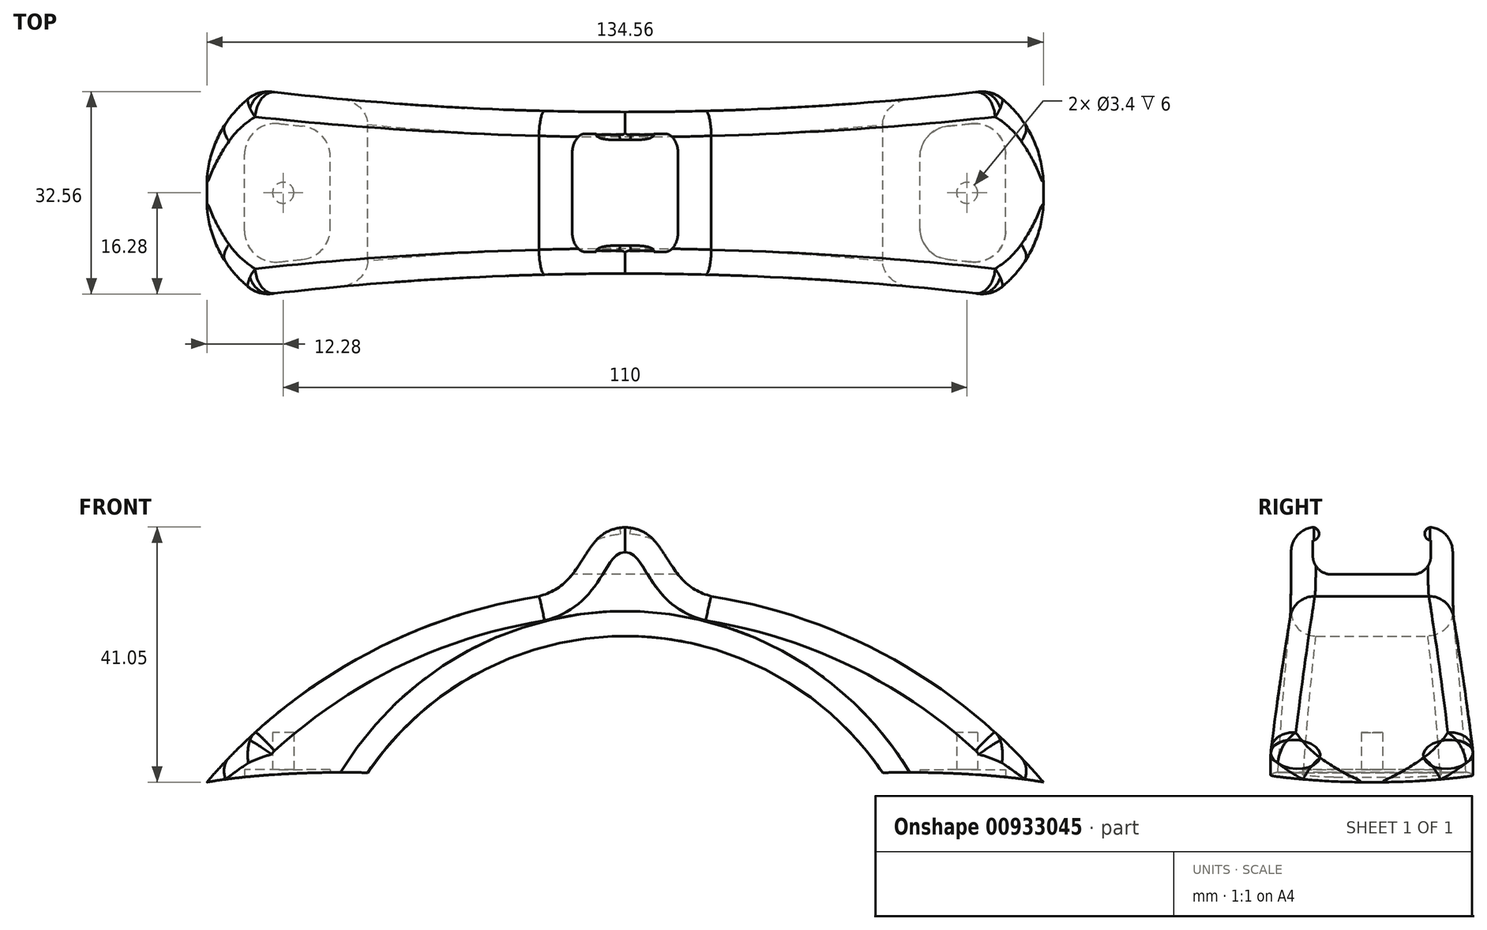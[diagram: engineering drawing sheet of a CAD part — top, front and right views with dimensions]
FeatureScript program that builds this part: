
annotation { "Feature Type Name" : "Feature", "Feature Type Description" : "" }
export const myFeature = defineFeature(function(context is Context, id is Id, definition is map)
    precondition{}
    {
        {
            var Q0;
            Q0=qCreatedBy(makeId("Front.planeOp"),FACE);
            var sketch = newSketch(context, id + "F0", { "sketchPlane" : qUnion([Q0])});
            skCircle(sketch, "E0", {"center": v(0, -26.5) * mm, "radius": 50 * mm});
            skCircle(sketch, "E1", {"center": v(0, -57.5) * mm, "radius": 88.5 * mm});
            skSolve(sketch);
        }
        {
            var Q0;
            Q0 = qSketchRegion(id + "F0", true);
            var Q1;
            Q1 = qSketchRegion(id + "F2", true);
            extrude(context, id + "F1", {"entities" : qUnion([Q0, Q1]), "flatOperationType" : FlatOperationType.REMOVE, "endBound" : BoundingType.SYMMETRIC, "depth" : 35 * mm, "offsetDistance" : 25 * mm, "domain" : OperationDomain.MODEL});
        }
        {
            var Q0;
            Q0=qCreatedBy(makeId("Top.planeOp"),FACE);
            var sketch = newSketch(context, id + "F2", { "sketchPlane" : qUnion([Q0])});
            skLineSegment(sketch, "E2.bottom", {"start": v(69.4, -44.81) * mm, "end": v(-70.4, -44.81) * mm});
            skLineSegment(sketch, "E2.top", {"start": v(69.4, 50.02) * mm, "end": v(-70.4, 50.02) * mm});
            skLineSegment(sketch, "E2.left", {"start": v(69.4, -44.81) * mm, "end": v(69.4, 50.02) * mm});
            skLineSegment(sketch, "E2.right", {"start": v(-70.4, -44.81) * mm, "end": v(-70.4, 50.02) * mm});
            skSolve(sketch);
        }
        {
            var Q0;
            Q0 = qSketchRegion(id + "F2", true);
            extrude(context, id + "F3", {"entities" : qUnion([Q0]), "operationType" : NewBodyOperationType.INTERSECT, "depth" : 50 * mm, "offsetDistance" : 25 * mm});
        }
        {
            var Q0;
            Q0=qCreatedBy(makeId("Top.planeOp"),FACE);
            var sketch = newSketch(context, id + "F4", { "sketchPlane" : qUnion([Q0])});
            skArc(sketch, "E3", {"start": v(-67.28, 0) * mm, "mid": v(-64.75, -10.32) * mm, "end": v(-56.92, -17.5) * mm});
            skLineSegment(sketch, "E4", {"start": v(-67.28, 0) * mm, "end": v(-74.97, -22.14) * mm});
            skLineSegment(sketch, "E5", {"start": v(-74.97, -22.14) * mm, "end": v(-56.92, -17.5) * mm});
            skLineSegment(sketch, "E6.MirrorCS", {"start": v(-67.28, 0) * mm, "end": v(-74.97, 22.14) * mm});
            skLineSegment(sketch, "E7.MirrorCS", {"start": v(-74.97, 22.14) * mm, "end": v(-56.92, 17.5) * mm});
            skArc(sketch, "E8.MirrorCS", {"start": v(-67.28, 0) * mm, "mid": v(-64.75, 10.32) * mm, "end": v(-56.92, 17.5) * mm});
            skLineSegment(sketch, "E9.MirrorCS", {"start": v(74.97, 22.14) * mm, "end": v(56.92, 17.5) * mm});
            skLineSegment(sketch, "E10.MirrorCS", {"start": v(67.28, 0) * mm, "end": v(74.97, 22.14) * mm});
            skArc(sketch, "E11.MirrorCS", {"start": v(67.28, 0) * mm, "mid": v(64.75, 10.32) * mm, "end": v(56.92, 17.5) * mm});
            skLineSegment(sketch, "E12.MirrorCS", {"start": v(67.28, 0) * mm, "end": v(74.97, -22.14) * mm});
            skArc(sketch, "E13.MirrorCS", {"start": v(67.28, 0) * mm, "mid": v(64.75, -10.32) * mm, "end": v(56.92, -17.5) * mm});
            skLineSegment(sketch, "E14.MirrorCS", {"start": v(74.97, -22.14) * mm, "end": v(56.92, -17.5) * mm});
            skSolve(sketch);
        }
        {
            var Q0;
            Q0=qCreatedBy(makeId("Top.planeOp"),FACE);
            var sketch = newSketch(context, id + "F5", { "sketchPlane" : qUnion([Q0])});
            skCircle(sketch, "E15", {"center": v(-55, 0) * mm, "radius": 1.7 * mm});
            skCircle(sketch, "E16", {"center": v(55, 0) * mm, "radius": 1.7 * mm});
            skSolve(sketch);
        }
        {
            var Q0;
            Q0 = qSketchRegion(id + "F5", true);
            extrude(context, id + "F6", {"entities" : qUnion([Q0]), "operationType" : NewBodyOperationType.REMOVE, "depth" : 8 * mm, "hasOffset" : true, "offsetDistance" : 10 * mm});
        }
        {
            var Q0;
            Q0=qCreatedBy(makeId("Front.planeOp"),FACE);
            var sketch = newSketch(context, id + "F7", { "sketchPlane" : qUnion([Q0])});
            skLineSegment(sketch, "E17", {"start": v(-41.42, 1.5) * mm, "end": v(-41.42, 0) * mm});
            skLineSegment(sketch, "E18", {"start": v(-41.42, 0) * mm, "end": v(-67.22, 0) * mm});
            skLineSegment(sketch, "E19.MirrorCS", {"start": v(41.42, 1.5) * mm, "end": v(41.42, 0) * mm});
            skLineSegment(sketch, "E20.MirrorCS", {"start": v(41.42, 0) * mm, "end": v(67.22, 0) * mm});
            skFitSpline(sketch, "E21", {"points": [v(-41.42, 1.5) * mm, v(-67.22, 0) * mm], "startDerivative": vector(-16.27, 0.6) * mm, "endDerivative": vector(-25.43, -4.49) * mm});
            skFitSpline(sketch, "E22.MirrorCS", {"points": [v(41.42, 1.5) * mm, v(67.22, 0) * mm], "startDerivative": vector(16.27, 0.6) * mm, "endDerivative": vector(25.43, -4.49) * mm});
            skSolve(sketch);
        }
        {
            var Q0;
            Q0 = qSketchRegion(id + "F7", true);
            extrude(context, id + "F8", {"entities" : qUnion([Q0]), "operationType" : NewBodyOperationType.REMOVE, "endBound" : BoundingType.SYMMETRIC, "depth" : 40 * mm, "offsetDistance" : 25 * mm});
        }
        {
            var Q0;
            Q0=qCreatedBy(makeId("Front.planeOp"),FACE);
            var sketch = newSketch(context, id + "F9", { "sketchPlane" : qUnion([Q0])});
            skCircle(sketch, "E23", {"center": v(0, 36) * mm, "radius": 5 * mm});
            skFitSpline(sketch, "E24", {"points": [v(0, 41) * mm, v(-15.85, 29.57) * mm], "startDerivative": vector(-23.74, -0.9) * mm, "endDerivative": vector(-30.85, -2.99) * mm});
            skFitSpline(sketch, "E25.MirrorCS", {"points": [v(0, 41) * mm, v(15.85, 29.57) * mm], "startDerivative": vector(23.74, -0.9) * mm, "endDerivative": vector(30.85, -2.99) * mm});
            skLineSegment(sketch, "E26", {"start": v(-15.85, 29.57) * mm, "end": v(15.85, 29.57) * mm});
            skSolve(sketch);
        }
        {
            var Q0;
            Q0 = qSketchRegion(id + "F9", true);
            extrude(context, id + "F10", {"entities" : qUnion([Q0]), "operationType" : NewBodyOperationType.ADD, "endBound" : BoundingType.SYMMETRIC, "depth" : 35 * mm, "offsetDistance" : 25 * mm});
        }
        {
            var Q0;
            Q0=qCreatedBy(makeId("Top.planeOp"),FACE);
            var sketch = newSketch(context, id + "F11", { "sketchPlane" : qUnion([Q0])});
            skCircle(sketch, "E27", {"center": v(0, -513) * mm, "radius": 500 * mm});
            skCircle(sketch, "E28.MirrorC", {"center": v(0, 513) * mm, "radius": 500 * mm});
            skSolve(sketch);
        }
        {
            var Q0;
            Q0 = qSketchRegion(id + "F11", true);
            extrude(context, id + "F12", {"entities" : qUnion([Q0]), "operationType" : NewBodyOperationType.REMOVE, "depth" : 50 * mm, "offsetDistance" : 25 * mm});
        }
        {
            var Q0;
            Q0=qCreatedBy(makeId("Right.planeOp"),FACE);
            var sketch = newSketch(context, id + "F13", { "sketchPlane" : qUnion([Q0])});
            skLineSegment(sketch, "E29.bottom", {"start": v(9.5, 33.42) * mm, "end": v(-9.5, 33.42) * mm});
            skLineSegment(sketch, "E29.top", {"start": v(9.5, 38.92) * mm, "end": v(-9.5, 38.92) * mm});
            skLineSegment(sketch, "E29.left", {"start": v(9.5, 33.42) * mm, "end": v(9.5, 38.92) * mm});
            skLineSegment(sketch, "E29.right", {"start": v(-9.5, 33.42) * mm, "end": v(-9.5, 38.92) * mm});
            skPoint(sketch, "E30.middle", {"position": v(0, 36.17) * mm});
            skLineSegment(sketch, "E31.bottom", {"start": v(-8.5, 38.92) * mm, "end": v(8.5, 38.92) * mm});
            skLineSegment(sketch, "E31.top", {"start": v(-8.5, 41.92) * mm, "end": v(8.5, 41.92) * mm});
            skLineSegment(sketch, "E31.left", {"start": v(-8.5, 38.92) * mm, "end": v(-8.5, 41.92) * mm});
            skLineSegment(sketch, "E31.right", {"start": v(8.5, 38.92) * mm, "end": v(8.5, 41.92) * mm});
            skSolve(sketch);
        }
        {
            var Q0;
            Q0 = qSketchRegion(id + "F13", true);
            extrude(context, id + "F14", {"entities" : qUnion([Q0]), "operationType" : NewBodyOperationType.REMOVE, "endBound" : BoundingType.SYMMETRIC, "depth" : 25 * mm, "offsetDistance" : 25 * mm});
        }
        {
            var Q0;
            Q0=qCreatedBy(makeId("Top.planeOp"),FACE);
            var sketch = newSketch(context, id + "F15", { "sketchPlane" : qUnion([Q0])});
            skLineSegment(sketch, "E32", {"start": v(55.68, 11.13) * mm, "end": v(51.89, 10.71) * mm});
            skLineSegment(sketch, "E33.MirrorCS", {"start": v(55.68, -11.13) * mm, "end": v(51.89, -10.71) * mm});
            skLineSegment(sketch, "E34", {"start": v(47.42, 5.74) * mm, "end": v(47.42, -5.74) * mm});
            skLineSegment(sketch, "E35", {"start": v(61.22, 6.15) * mm, "end": v(61.22, -6.15) * mm});
            skLineSegment(sketch, "E36.MirrorCS", {"start": v(-47.42, 5.74) * mm, "end": v(-47.42, -5.74) * mm});
            skLineSegment(sketch, "E37.MirrorCS", {"start": v(-55.68, 11.13) * mm, "end": v(-51.89, 10.71) * mm});
            skLineSegment(sketch, "E38.MirrorCS", {"start": v(-61.22, 6.15) * mm, "end": v(-61.22, -6.15) * mm});
            skLineSegment(sketch, "E39.MirrorCS", {"start": v(-55.68, -11.13) * mm, "end": v(-51.89, -10.71) * mm});
            skPoint(sketch, "E40.visualSharp", {"position": v(47.42, -10.23) * mm});
            skArc(sketch, "E40.filletArc", {"start": v(47.42, -5.74) * mm, "mid": v(48.7, -9.08) * mm, "end": v(51.89, -10.71) * mm});
            skPoint(sketch, "E41.visualSharp", {"position": v(61.22, -11.72) * mm});
            skArc(sketch, "E41.filletArc", {"start": v(55.68, -11.13) * mm, "mid": v(59.56, -9.87) * mm, "end": v(61.22, -6.15) * mm});
            skPoint(sketch, "E42.visualSharp", {"position": v(47.42, 10.23) * mm});
            skArc(sketch, "E42.filletArc", {"start": v(51.89, 10.71) * mm, "mid": v(48.7, 9.08) * mm, "end": v(47.42, 5.74) * mm});
            skPoint(sketch, "E43.visualSharp", {"position": v(61.22, 11.72) * mm});
            skArc(sketch, "E43.filletArc", {"start": v(61.22, 6.15) * mm, "mid": v(59.56, 9.87) * mm, "end": v(55.68, 11.13) * mm});
            skPoint(sketch, "E44.visualSharp", {"position": v(-47.42, -10.23) * mm});
            skArc(sketch, "E44.filletArc", {"start": v(-51.89, -10.71) * mm, "mid": v(-48.7, -9.08) * mm, "end": v(-47.42, -5.74) * mm});
            skPoint(sketch, "E45.visualSharp", {"position": v(-47.42, 10.23) * mm});
            skArc(sketch, "E45.filletArc", {"start": v(-47.42, 5.74) * mm, "mid": v(-48.7, 9.08) * mm, "end": v(-51.89, 10.71) * mm});
            skPoint(sketch, "E46.visualSharp", {"position": v(-61.22, 11.72) * mm});
            skArc(sketch, "E46.filletArc", {"start": v(-55.68, 11.13) * mm, "mid": v(-59.56, 9.87) * mm, "end": v(-61.22, 6.15) * mm});
            skPoint(sketch, "E47.visualSharp", {"position": v(-61.22, -11.72) * mm});
            skArc(sketch, "E47.filletArc", {"start": v(-61.22, -6.15) * mm, "mid": v(-59.56, -9.87) * mm, "end": v(-55.68, -11.13) * mm});
            skSolve(sketch);
        }
        {
            var Q0;
            Q0=makeQuery(id+"F14.boolean.opBoolean","COPY",EDGE,{"derivedFrom":makeQuery(id+"F14.opExtrude","SWEPT_EDGE",EDGE,{"disambiguationData":[OSD([sQuery(id+"F13.wireOp",EDGE,"E29.bottom"),sQuery(id+"F13.wireOp",EDGE,"E29.right")])]})});
            var Q1;
            Q1=makeQuery(id+"F14.boolean.opBoolean","COPY",EDGE,{"derivedFrom":makeQuery(id+"F14.opExtrude","SWEPT_EDGE",EDGE,{"disambiguationData":[OSD([sQuery(id+"F13.wireOp",EDGE,"E29.bottom"),sQuery(id+"F13.wireOp",EDGE,"E29.left")])]})});
            fillet(context, id + "F16", {"entities" : qUnion([Q0, Q1]), "radius" : 3 * mm, "tangentPropagation" : true, "allowEdgeOverflow" : false});
        }
        {
            var Q0;
            Q0=makeQuery(id+"F14.boolean.opBoolean","INTERSECT",EDGE,{"derivedFrom":[makeQuery(id+"F10.opExtrude","SWEPT_FACE",FACE,{"disambiguationData":[OSD([sQuery(id+"F9.wireOp",EDGE,"E24")])]}),makeQuery(id+"F14.opExtrude","SWEPT_FACE",FACE,{"disambiguationData":[OSD([sQuery(id+"F13.wireOp",EDGE,"E31.left")])]})]});
            var Q1;
            Q1=makeQuery(id+"F14.boolean.opBoolean","INTERSECT",EDGE,{"derivedFrom":[makeQuery(id+"F10.opExtrude","SWEPT_FACE",FACE,{"disambiguationData":[OSD([sQuery(id+"F9.wireOp",EDGE,"E25.MirrorCS")])]}),makeQuery(id+"F14.opExtrude","SWEPT_FACE",FACE,{"disambiguationData":[OSD([sQuery(id+"F13.wireOp",EDGE,"E31.left")])]})]});
            var Q2;
            Q2=makeQuery(id+"F14.boolean.opBoolean","INTERSECT",EDGE,{"derivedFrom":[makeQuery(id+"F10.opExtrude","SWEPT_FACE",FACE,{"disambiguationData":[OSD([sQuery(id+"F9.wireOp",EDGE,"E23")])]}),makeQuery(id+"F14.opExtrude","SWEPT_FACE",FACE,{"disambiguationData":[OSD([sQuery(id+"F13.wireOp",EDGE,"E31.left")])]})]});
            var Q3;
            Q3=makeQuery(id+"F14.boolean.opBoolean","INTERSECT",EDGE,{"derivedFrom":[makeQuery(id+"F10.opExtrude","SWEPT_FACE",FACE,{"disambiguationData":[OSD([sQuery(id+"F9.wireOp",EDGE,"E25.MirrorCS")])]}),makeQuery(id+"F14.opExtrude","SWEPT_FACE",FACE,{"disambiguationData":[OSD([sQuery(id+"F13.wireOp",EDGE,"E31.right")])]})]});
            var Q4;
            Q4=makeQuery(id+"F14.boolean.opBoolean","INTERSECT",EDGE,{"derivedFrom":[makeQuery(id+"F10.opExtrude","SWEPT_FACE",FACE,{"disambiguationData":[OSD([sQuery(id+"F9.wireOp",EDGE,"E23")])]}),makeQuery(id+"F14.opExtrude","SWEPT_FACE",FACE,{"disambiguationData":[OSD([sQuery(id+"F13.wireOp",EDGE,"E31.right")])]})]});
            var Q5;
            Q5=makeQuery(id+"F14.boolean.opBoolean","COPY",EDGE,{"derivedFrom":makeQuery(id+"F14.opExtrude","SWEPT_EDGE",EDGE,{"disambiguationData":[OSD([sQuery(id+"F13.wireOp",EDGE,"E29.top"),sQuery(id+"F13.wireOp",EDGE,"E31.bottom"),sQuery(id+"F13.wireOp",EDGE,"E31.left")])]})});
            var Q6;
            Q6=makeQuery(id+"F14.boolean.opBoolean","COPY",EDGE,{"derivedFrom":makeQuery(id+"F14.opExtrude","SWEPT_EDGE",EDGE,{"disambiguationData":[OSD([sQuery(id+"F13.wireOp",EDGE,"E29.top"),sQuery(id+"F13.wireOp",EDGE,"E31.bottom"),sQuery(id+"F13.wireOp",EDGE,"E31.right")])]})});
            var Q7;
            Q7=makeQuery(id+"F14.boolean.opBoolean","INTERSECT",EDGE,{"derivedFrom":[makeQuery(id+"F10.opExtrude","SWEPT_FACE",FACE,{"disambiguationData":[OSD([sQuery(id+"F9.wireOp",EDGE,"E24")])]}),makeQuery(id+"F14.opExtrude","SWEPT_FACE",FACE,{"disambiguationData":[OSD([sQuery(id+"F13.wireOp",EDGE,"E31.right")])]})]});
            fillet(context, id + "F17", {"entities" : qUnion([Q0, Q1, Q2, Q3, Q4, Q5, Q6, Q7]), "radius" : 1 * mm, "tangentPropagation" : true, "allowEdgeOverflow" : false});
        }
        {
            var Q0;
            Q0=makeQuery(id+"F12.boolean.opBoolean","INTERSECT",EDGE,{"derivedFrom":[makeQuery(id+"F10.opExtrude","SWEPT_FACE",FACE,{"disambiguationData":[OSD([sQuery(id+"F9.wireOp",EDGE,"E25.MirrorCS")])]}),makeQuery(id+"F12.opExtrude","SWEPT_FACE",FACE,{"disambiguationData":[OSD([sQuery(id+"F11.wireOp",EDGE,"E28.MirrorC")])]})]});
            var Q1;
            Q1=makeQuery(id+"F12.boolean.opBoolean","INTERSECT",EDGE,{"derivedFrom":[makeQuery(id+"F10.opExtrude","SWEPT_FACE",FACE,{"disambiguationData":[OSD([sQuery(id+"F9.wireOp",EDGE,"E23")])]}),makeQuery(id+"F12.opExtrude","SWEPT_FACE",FACE,{"disambiguationData":[OSD([sQuery(id+"F11.wireOp",EDGE,"E28.MirrorC")])]})]});
            var Q2;
            Q2=makeQuery(id+"F12.boolean.opBoolean","INTERSECT",EDGE,{"derivedFrom":[makeQuery(id+"F10.opExtrude","SWEPT_FACE",FACE,{"disambiguationData":[OSD([sQuery(id+"F9.wireOp",EDGE,"E24")])]}),makeQuery(id+"F12.opExtrude","SWEPT_FACE",FACE,{"disambiguationData":[OSD([sQuery(id+"F11.wireOp",EDGE,"E28.MirrorC")])]})]});
            var Q3;
            Q3=makeQuery(id+"F12.boolean.opBoolean","INTERSECT",EDGE,{"derivedFrom":[makeQuery(id+"F10.opExtrude","SWEPT_FACE",FACE,{"disambiguationData":[OSD([sQuery(id+"F9.wireOp",EDGE,"E25.MirrorCS")])]}),makeQuery(id+"F12.opExtrude","SWEPT_FACE",FACE,{"disambiguationData":[OSD([sQuery(id+"F11.wireOp",EDGE,"E27")])]})]});
            var Q4;
            Q4=makeQuery(id+"F12.boolean.opBoolean","INTERSECT",EDGE,{"derivedFrom":[makeQuery(id+"F10.opExtrude","SWEPT_FACE",FACE,{"disambiguationData":[OSD([sQuery(id+"F9.wireOp",EDGE,"E24")])]}),makeQuery(id+"F12.opExtrude","SWEPT_FACE",FACE,{"disambiguationData":[OSD([sQuery(id+"F11.wireOp",EDGE,"E27")])]})]});
            var Q5;
            Q5=makeQuery(id+"F12.boolean.opBoolean","INTERSECT",EDGE,{"derivedFrom":[makeQuery(id+"F10.opExtrude","SWEPT_FACE",FACE,{"disambiguationData":[OSD([sQuery(id+"F9.wireOp",EDGE,"E23")])]}),makeQuery(id+"F12.opExtrude","SWEPT_FACE",FACE,{"disambiguationData":[OSD([sQuery(id+"F11.wireOp",EDGE,"E27")])]})]});
            var Q6;
            Q6=makeQuery(id+"F12.boolean.opBoolean","INTERSECT",EDGE,{"derivedFrom":[makeQuery(id+"F1.opExtrude","SWEPT_FACE",FACE,{"disambiguationData":[OSD([sQuery(id+"F0.wireOp",EDGE,"E0")])]}),makeQuery(id+"F12.opExtrude","SWEPT_FACE",FACE,{"disambiguationData":[OSD([sQuery(id+"F11.wireOp",EDGE,"E27")])]})]});
            var Q7;
            Q7=makeQuery(id+"F12.boolean.opBoolean","INTERSECT",EDGE,{"derivedFrom":[makeQuery(id+"F1.opExtrude","SWEPT_FACE",FACE,{"disambiguationData":[OSD([sQuery(id+"F0.wireOp",EDGE,"E0")])]}),makeQuery(id+"F12.opExtrude","SWEPT_FACE",FACE,{"disambiguationData":[OSD([sQuery(id+"F11.wireOp",EDGE,"E28.MirrorC")])]})]});
            var Q8;
            {var subQ2=sQuery(id+"F9.wireOp",EDGE,"E24");var subQ4=sQuery(id+"F0.wireOp",EDGE,"E1");Q8=makeQuery(id+"F12.boolean.opBoolean","INTERSECT",EDGE,{"derivedFrom":[makeQuery(id+"F10.boolean.opBoolean","SPLIT",FACE,{"disambiguationData":[TD([makeQuery(id+"F10.opExtrude","SWEPT_FACE",FACE,{"disambiguationData":[OSD([subQ2])]})])],"derivedFrom":makeQuery(id+"F1.opExtrude","SWEPT_FACE",FACE,{"disambiguationData":[OSD([subQ4])]})}),makeQuery(id+"F12.opExtrude","SWEPT_FACE",FACE,{"disambiguationData":[OSD([sQuery(id+"F11.wireOp",EDGE,"E27")])]})]});}
            var Q9;
            {var subQ2=sQuery(id+"F9.wireOp",EDGE,"E24");var subQ4=sQuery(id+"F0.wireOp",EDGE,"E1");Q9=makeQuery(id+"F12.boolean.opBoolean","INTERSECT",EDGE,{"derivedFrom":[makeQuery(id+"F10.boolean.opBoolean","SPLIT",FACE,{"disambiguationData":[TD([makeQuery(id+"F10.opExtrude","SWEPT_FACE",FACE,{"disambiguationData":[OSD([subQ2])]})])],"derivedFrom":makeQuery(id+"F1.opExtrude","SWEPT_FACE",FACE,{"disambiguationData":[OSD([subQ4])]})}),makeQuery(id+"F12.opExtrude","SWEPT_FACE",FACE,{"disambiguationData":[OSD([sQuery(id+"F11.wireOp",EDGE,"E28.MirrorC")])]})]});}
            var Q10;
            {var subQ1=sQuery(id+"F9.wireOp",EDGE,"E25.MirrorCS");var subQ4=sQuery(id+"F0.wireOp",EDGE,"E1");Q10=makeQuery(id+"F12.boolean.opBoolean","INTERSECT",EDGE,{"derivedFrom":[makeQuery(id+"F10.boolean.opBoolean","SPLIT",FACE,{"disambiguationData":[TD([makeQuery(id+"F10.opExtrude","SWEPT_FACE",FACE,{"disambiguationData":[OSD([subQ1])]})])],"derivedFrom":makeQuery(id+"F1.opExtrude","SWEPT_FACE",FACE,{"disambiguationData":[OSD([subQ4])]})}),makeQuery(id+"F12.opExtrude","SWEPT_FACE",FACE,{"disambiguationData":[OSD([sQuery(id+"F11.wireOp",EDGE,"E28.MirrorC")])]})]});}
            var Q11;
            {var subQ1=sQuery(id+"F9.wireOp",EDGE,"E25.MirrorCS");var subQ4=sQuery(id+"F0.wireOp",EDGE,"E1");Q11=makeQuery(id+"F12.boolean.opBoolean","INTERSECT",EDGE,{"derivedFrom":[makeQuery(id+"F10.boolean.opBoolean","SPLIT",FACE,{"disambiguationData":[TD([makeQuery(id+"F10.opExtrude","SWEPT_FACE",FACE,{"disambiguationData":[OSD([subQ1])]})])],"derivedFrom":makeQuery(id+"F1.opExtrude","SWEPT_FACE",FACE,{"disambiguationData":[OSD([subQ4])]})}),makeQuery(id+"F12.opExtrude","SWEPT_FACE",FACE,{"disambiguationData":[OSD([sQuery(id+"F11.wireOp",EDGE,"E27")])]})]});}
            fillet(context, id + "F18", {"entities" : qUnion([Q0, Q1, Q2, Q3, Q4, Q5, Q6, Q7, Q8, Q9, Q10, Q11]), "radius" : 4 * mm, "tangentPropagation" : true, "allowEdgeOverflow" : false});
        }
        {
            var Q0;
            Q0 = qSketchRegion(id + "F15", true);
            extrude(context, id + "F19", {"entities" : qUnion([Q0]), "operationType" : NewBodyOperationType.REMOVE, "depth" : 2 * mm, "offsetDistance" : 25 * mm});
        }
        {
            var Q0;
            Q0 = qSketchRegion(id + "F4", true);
            extrude(context, id + "F20", {"entities" : qUnion([Q0]), "operationType" : NewBodyOperationType.REMOVE, "depth" : 25 * mm, "offsetDistance" : 25 * mm});
        }
        {
            var Q0;
            Q0=makeQuery(id+"F20.boolean.opBoolean","INTERSECT",EDGE,{"derivedFrom":[makeQuery(id+"F12.boolean.opBoolean","COPY",FACE,{"derivedFrom":makeQuery(id+"F12.opExtrude","SWEPT_FACE",FACE,{"disambiguationData":[OSD([sQuery(id+"F11.wireOp",EDGE,"E28.MirrorC")])]})}),makeQuery(id+"F20.opExtrude","SWEPT_FACE",FACE,{"disambiguationData":[OSD([sQuery(id+"F4.wireOp",EDGE,"E8.MirrorCS")])]})]});
            var Q1;
            {var subQ0=sQuery(id+"F11.wireOp",EDGE,"E28.MirrorC");var subQ3=sQuery(id+"F9.wireOp",EDGE,"E24");var subQ5=sQuery(id+"F0.wireOp",EDGE,"E1");Q1=makeQuery(id+"F20.boolean.opBoolean","INTERSECT",EDGE,{"derivedFrom":[makeQuery(id+"F18.opFillet","BLEND_FACE",FACE,{"disambiguationData":[OSD([subQ5,subQ0]),TDD([makeQuery(id+"F12.boolean.opBoolean","INTERSECT",EDGE,{"derivedFrom":[makeQuery(id+"F10.boolean.opBoolean","SPLIT",FACE,{"disambiguationData":[TD([makeQuery(id+"F10.opExtrude","SWEPT_FACE",FACE,{"disambiguationData":[OSD([subQ3])]})])],"derivedFrom":makeQuery(id+"F1.opExtrude","SWEPT_FACE",FACE,{"disambiguationData":[OSD([subQ5])]})}),makeQuery(id+"F12.opExtrude","SWEPT_FACE",FACE,{"disambiguationData":[OSD([subQ0])]})]})])]}),makeQuery(id+"F20.opExtrude","SWEPT_FACE",FACE,{"disambiguationData":[OSD([sQuery(id+"F4.wireOp",EDGE,"E8.MirrorCS")])]})]});}
            var Q2;
            {var subQ2=sQuery(id+"F9.wireOp",EDGE,"E24");var subQ4=sQuery(id+"F0.wireOp",EDGE,"E1");Q2=makeQuery(id+"F20.boolean.opBoolean","INTERSECT",EDGE,{"derivedFrom":[makeQuery(id+"F10.boolean.opBoolean","SPLIT",FACE,{"disambiguationData":[TD([makeQuery(id+"F10.opExtrude","SWEPT_FACE",FACE,{"disambiguationData":[OSD([subQ2])]})])],"derivedFrom":makeQuery(id+"F1.opExtrude","SWEPT_FACE",FACE,{"disambiguationData":[OSD([subQ4])]})}),makeQuery(id+"F20.opExtrude","SWEPT_FACE",FACE,{"disambiguationData":[OSD([sQuery(id+"F4.wireOp",EDGE,"E8.MirrorCS")])]})]});}
            var Q3;
            {var subQ2=sQuery(id+"F9.wireOp",EDGE,"E24");var subQ4=sQuery(id+"F0.wireOp",EDGE,"E1");Q3=makeQuery(id+"F20.boolean.opBoolean","INTERSECT",EDGE,{"derivedFrom":[makeQuery(id+"F10.boolean.opBoolean","SPLIT",FACE,{"disambiguationData":[TD([makeQuery(id+"F10.opExtrude","SWEPT_FACE",FACE,{"disambiguationData":[OSD([subQ2])]})])],"derivedFrom":makeQuery(id+"F1.opExtrude","SWEPT_FACE",FACE,{"disambiguationData":[OSD([subQ4])]})}),makeQuery(id+"F20.opExtrude","SWEPT_FACE",FACE,{"disambiguationData":[OSD([sQuery(id+"F4.wireOp",EDGE,"E3")])]})]});}
            var Q4;
            {var subQ0=sQuery(id+"F11.wireOp",EDGE,"E27");var subQ3=sQuery(id+"F9.wireOp",EDGE,"E24");var subQ5=sQuery(id+"F0.wireOp",EDGE,"E1");Q4=makeQuery(id+"F20.boolean.opBoolean","INTERSECT",EDGE,{"derivedFrom":[makeQuery(id+"F18.opFillet","BLEND_FACE",FACE,{"disambiguationData":[OSD([subQ5,subQ0]),TDD([makeQuery(id+"F12.boolean.opBoolean","INTERSECT",EDGE,{"derivedFrom":[makeQuery(id+"F10.boolean.opBoolean","SPLIT",FACE,{"disambiguationData":[TD([makeQuery(id+"F10.opExtrude","SWEPT_FACE",FACE,{"disambiguationData":[OSD([subQ3])]})])],"derivedFrom":makeQuery(id+"F1.opExtrude","SWEPT_FACE",FACE,{"disambiguationData":[OSD([subQ5])]})}),makeQuery(id+"F12.opExtrude","SWEPT_FACE",FACE,{"disambiguationData":[OSD([subQ0])]})]})])]}),makeQuery(id+"F20.opExtrude","SWEPT_FACE",FACE,{"disambiguationData":[OSD([sQuery(id+"F4.wireOp",EDGE,"E3")])]})]});}
            var Q5;
            {var subQ1=sQuery(id+"F9.wireOp",EDGE,"E25.MirrorCS");var subQ4=sQuery(id+"F0.wireOp",EDGE,"E1");Q5=makeQuery(id+"F20.boolean.opBoolean","INTERSECT",EDGE,{"derivedFrom":[makeQuery(id+"F10.boolean.opBoolean","SPLIT",FACE,{"disambiguationData":[TD([makeQuery(id+"F10.opExtrude","SWEPT_FACE",FACE,{"disambiguationData":[OSD([subQ1])]})])],"derivedFrom":makeQuery(id+"F1.opExtrude","SWEPT_FACE",FACE,{"disambiguationData":[OSD([subQ4])]})}),makeQuery(id+"F20.opExtrude","SWEPT_FACE",FACE,{"disambiguationData":[OSD([sQuery(id+"F4.wireOp",EDGE,"E13.MirrorCS")])]})]});}
            var Q6;
            {var subQ0=sQuery(id+"F11.wireOp",EDGE,"E27");var subQ2=sQuery(id+"F9.wireOp",EDGE,"E25.MirrorCS");var subQ5=sQuery(id+"F0.wireOp",EDGE,"E1");Q6=makeQuery(id+"F20.boolean.opBoolean","INTERSECT",EDGE,{"derivedFrom":[makeQuery(id+"F18.opFillet","BLEND_FACE",FACE,{"disambiguationData":[OSD([subQ5,subQ0]),TDD([makeQuery(id+"F12.boolean.opBoolean","INTERSECT",EDGE,{"derivedFrom":[makeQuery(id+"F10.boolean.opBoolean","SPLIT",FACE,{"disambiguationData":[TD([makeQuery(id+"F10.opExtrude","SWEPT_FACE",FACE,{"disambiguationData":[OSD([subQ2])]})])],"derivedFrom":makeQuery(id+"F1.opExtrude","SWEPT_FACE",FACE,{"disambiguationData":[OSD([subQ5])]})}),makeQuery(id+"F12.opExtrude","SWEPT_FACE",FACE,{"disambiguationData":[OSD([subQ0])]})]})])]}),makeQuery(id+"F20.opExtrude","SWEPT_FACE",FACE,{"disambiguationData":[OSD([sQuery(id+"F4.wireOp",EDGE,"E13.MirrorCS")])]})]});}
            var Q7;
            Q7=makeQuery(id+"F20.boolean.opBoolean","INTERSECT",EDGE,{"derivedFrom":[makeQuery(id+"F12.boolean.opBoolean","COPY",FACE,{"derivedFrom":makeQuery(id+"F12.opExtrude","SWEPT_FACE",FACE,{"disambiguationData":[OSD([sQuery(id+"F11.wireOp",EDGE,"E27")])]})}),makeQuery(id+"F20.opExtrude","SWEPT_FACE",FACE,{"disambiguationData":[OSD([sQuery(id+"F4.wireOp",EDGE,"E13.MirrorCS")])]})]});
            var Q8;
            {var subQ1=sQuery(id+"F9.wireOp",EDGE,"E25.MirrorCS");var subQ4=sQuery(id+"F0.wireOp",EDGE,"E1");Q8=makeQuery(id+"F20.boolean.opBoolean","INTERSECT",EDGE,{"derivedFrom":[makeQuery(id+"F10.boolean.opBoolean","SPLIT",FACE,{"disambiguationData":[TD([makeQuery(id+"F10.opExtrude","SWEPT_FACE",FACE,{"disambiguationData":[OSD([subQ1])]})])],"derivedFrom":makeQuery(id+"F1.opExtrude","SWEPT_FACE",FACE,{"disambiguationData":[OSD([subQ4])]})}),makeQuery(id+"F20.opExtrude","SWEPT_FACE",FACE,{"disambiguationData":[OSD([sQuery(id+"F4.wireOp",EDGE,"E11.MirrorCS")])]})]});}
            var Q9;
            {var subQ0=sQuery(id+"F11.wireOp",EDGE,"E28.MirrorC");var subQ2=sQuery(id+"F9.wireOp",EDGE,"E25.MirrorCS");var subQ5=sQuery(id+"F0.wireOp",EDGE,"E1");Q9=makeQuery(id+"F20.boolean.opBoolean","INTERSECT",EDGE,{"derivedFrom":[makeQuery(id+"F18.opFillet","BLEND_FACE",FACE,{"disambiguationData":[OSD([subQ5,subQ0]),TDD([makeQuery(id+"F12.boolean.opBoolean","INTERSECT",EDGE,{"derivedFrom":[makeQuery(id+"F10.boolean.opBoolean","SPLIT",FACE,{"disambiguationData":[TD([makeQuery(id+"F10.opExtrude","SWEPT_FACE",FACE,{"disambiguationData":[OSD([subQ2])]})])],"derivedFrom":makeQuery(id+"F1.opExtrude","SWEPT_FACE",FACE,{"disambiguationData":[OSD([subQ5])]})}),makeQuery(id+"F12.opExtrude","SWEPT_FACE",FACE,{"disambiguationData":[OSD([subQ0])]})]})])]}),makeQuery(id+"F20.opExtrude","SWEPT_FACE",FACE,{"disambiguationData":[OSD([sQuery(id+"F4.wireOp",EDGE,"E11.MirrorCS")])]})]});}
            var Q10;
            Q10=makeQuery(id+"F20.boolean.opBoolean","INTERSECT",EDGE,{"derivedFrom":[makeQuery(id+"F12.boolean.opBoolean","COPY",FACE,{"derivedFrom":makeQuery(id+"F12.opExtrude","SWEPT_FACE",FACE,{"disambiguationData":[OSD([sQuery(id+"F11.wireOp",EDGE,"E28.MirrorC")])]})}),makeQuery(id+"F20.opExtrude","SWEPT_FACE",FACE,{"disambiguationData":[OSD([sQuery(id+"F4.wireOp",EDGE,"E11.MirrorCS")])]})]});
            var Q11;
            Q11=makeQuery(id+"F20.boolean.opBoolean","INTERSECT",EDGE,{"derivedFrom":[makeQuery(id+"F12.boolean.opBoolean","COPY",FACE,{"derivedFrom":makeQuery(id+"F12.opExtrude","SWEPT_FACE",FACE,{"disambiguationData":[OSD([sQuery(id+"F11.wireOp",EDGE,"E27")])]})}),makeQuery(id+"F20.opExtrude","SWEPT_FACE",FACE,{"disambiguationData":[OSD([sQuery(id+"F4.wireOp",EDGE,"E3")])]})]});
            fillet(context, id + "F21", {"entities" : qUnion([Q0, Q1, Q2, Q3, Q4, Q5, Q6, Q7, Q8, Q9, Q10, Q11]), "radius" : 5 * mm, "tangentPropagation" : true, "allowEdgeOverflow" : false});
        }
    });
